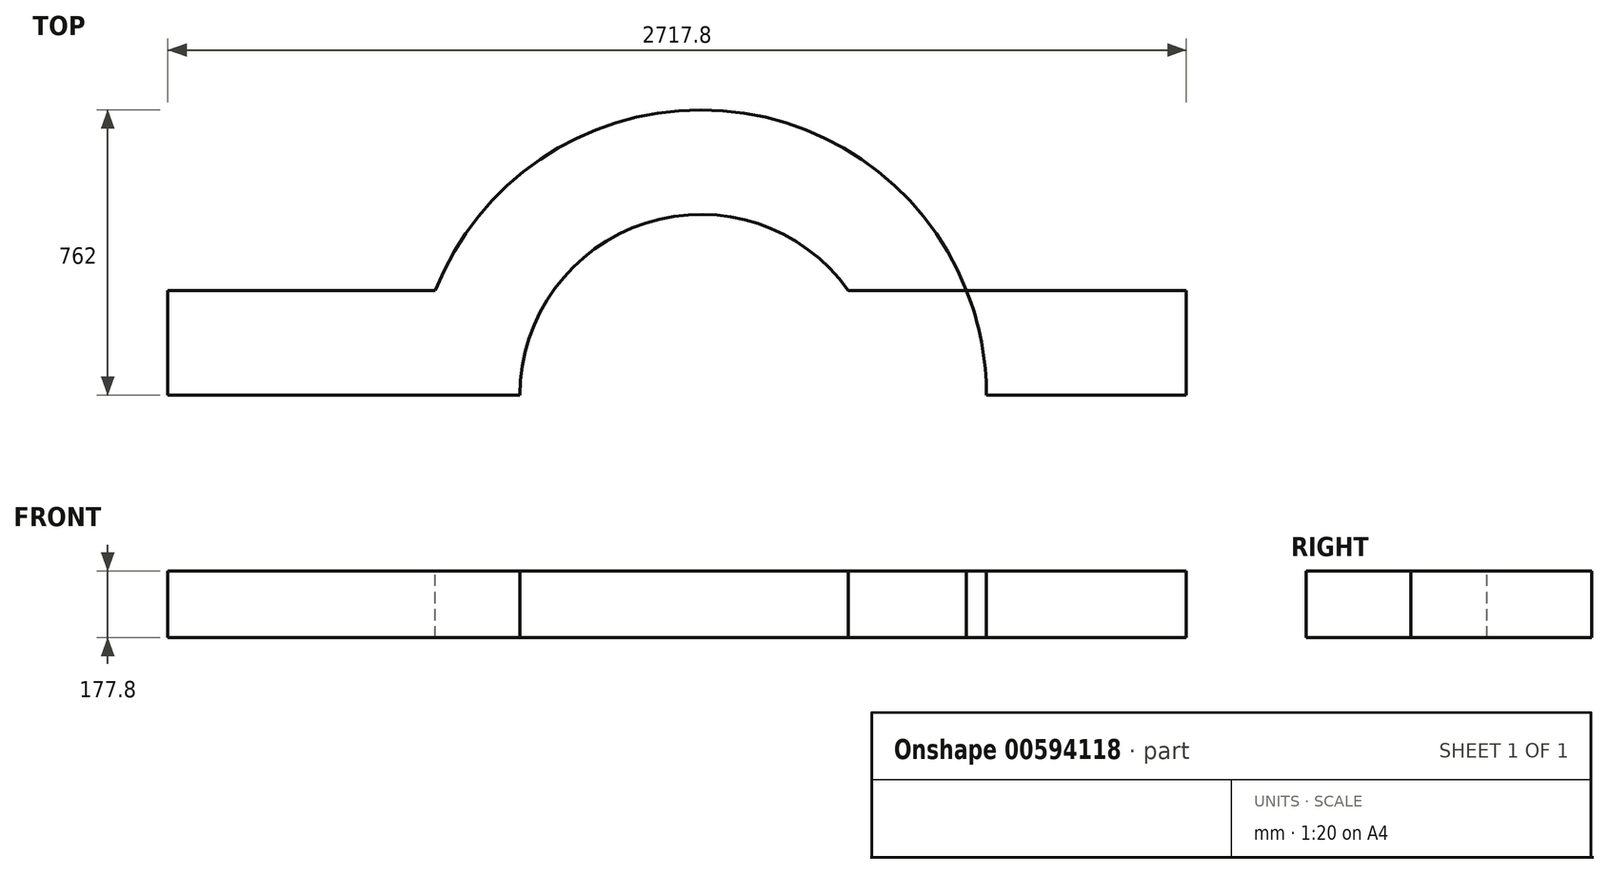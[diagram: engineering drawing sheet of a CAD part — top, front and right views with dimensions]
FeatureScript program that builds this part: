
annotation { "Feature Type Name" : "Feature", "Feature Type Description" : "" }
export const myFeature = defineFeature(function(context is Context, id is Id, definition is map)
    precondition{}
    {
        {
            var Q0;
            Q0=qCreatedBy(makeId("Top.planeOp"),FACE);
            var sketch = newSketch(context, id + "F0", { "sketchPlane" : qUnion([Q0])});
            skCircle(sketch, "E0", {"center": v(0, 0) * mm, "radius": 482.6 * mm});
            skCircle(sketch, "E1", {"center": v(0, 0) * mm, "radius": 762 * mm});
            skLineSegment(sketch, "E2.bottom", {"start": v(-1422.4, 279.4) * mm, "end": v(1295.4, 279.4) * mm});
            skLineSegment(sketch, "E2.top", {"start": v(-1422.4, 0) * mm, "end": v(1295.4, 0) * mm});
            skLineSegment(sketch, "E2.left", {"start": v(-1422.4, 279.4) * mm, "end": v(-1422.4, 0) * mm});
            skLineSegment(sketch, "E2.right", {"start": v(1295.4, 279.4) * mm, "end": v(1295.4, 0) * mm});
            skLineSegment(sketch, "E3.bottom", {"start": v(1295.4, 279.4) * mm, "end": v(1016, 279.4) * mm});
            skLineSegment(sketch, "E3.top", {"start": v(1295.4, 1320.8) * mm, "end": v(1016, 1320.8) * mm});
            skLineSegment(sketch, "E3.left", {"start": v(1295.4, 279.4) * mm, "end": v(1295.4, 1320.8) * mm});
            skLineSegment(sketch, "E3.right", {"start": v(1016, 279.4) * mm, "end": v(1016, 1320.8) * mm});
            skSolve(sketch);
        }
        {
            var Q0;
            {var subQ5=sQuery(id+"F0.wireOp",EDGE,"E2.left");Q0=makeQuery(id+"F0.imprint","IMPRINT",FACE,{"disambiguationData":[TD([[makeQuery(id+"F0.imprint","IMPRINT",EDGE,{"derivedFrom":subQ5}),1.0]])]});}
            var Q1;
            {var subQ0=sQuery(id+"F0.wireOp",EDGE,"E2.bottom");var subQ1=sQuery(id+"F0.wireOp",EDGE,"E0");var subQ2=makeQuery(id+"F0.imprint","INTERSECT",VERTEX,{"disambiguationData":[OD(1.0)],"derivedFrom":[subQ1,subQ0]});Q1=makeQuery(id+"F0.imprint","IMPRINT",FACE,{"disambiguationData":[TD([[makeQuery(id+"F0.imprint","IMPRINT",EDGE,{"disambiguationData":[TD([[subQ2,-1.0]])],"derivedFrom":subQ1}),-1.0]])]});}
            var Q2;
            {var subQ0=sQuery(id+"F0.wireOp",EDGE,"E2.bottom");var subQ1=sQuery(id+"F0.wireOp",EDGE,"E0");var subQ2=makeQuery(id+"F0.imprint","INTERSECT",VERTEX,{"disambiguationData":[OD(0.0)],"derivedFrom":[subQ1,subQ0]});Q2=makeQuery(id+"F0.imprint","IMPRINT",FACE,{"disambiguationData":[TD([[makeQuery(id+"F0.imprint","IMPRINT",EDGE,{"disambiguationData":[TD([[subQ2,1.0]])],"derivedFrom":subQ1}),-1.0]])]});}
            var Q3;
            {var subQ0=sQuery(id+"F0.wireOp",EDGE,"E2.right");Q3=makeQuery(id+"F0.imprint","IMPRINT",FACE,{"disambiguationData":[TD([[makeQuery(id+"F0.imprint","IMPRINT",EDGE,{"derivedFrom":subQ0}),-1.0]])]});}
            var Q4;
            Q4=makeQuery(id+"F0.imprint","IMPRINT",FACE,{"disambiguationData":[TD([[makeQuery(id+"F0.imprint","IMPRINT",EDGE,{"derivedFrom":sQuery(id+"F0.wireOp",EDGE,"E3.bottom")}),-1.0]])]});
            var Q5;
            {var subQ0=sQuery(id+"F0.wireOp",EDGE,"E2.bottom");var subQ1=sQuery(id+"F0.wireOp",EDGE,"E0");var subQ2=makeQuery(id+"F0.imprint","INTERSECT",VERTEX,{"disambiguationData":[OD(0.0)],"derivedFrom":[subQ1,subQ0]});Q5=makeQuery(id+"F0.imprint","IMPRINT",FACE,{"disambiguationData":[TD([[makeQuery(id+"F0.imprint","IMPRINT",EDGE,{"disambiguationData":[TD([[subQ2,-1.0]])],"derivedFrom":subQ1}),-1.0]])]});}
            extrude(context, id + "F1", {"entities" : qUnion([Q0, Q1, Q2, Q3, Q4, Q5]), "oppositeDirection" : true, "depth" : 177.8 * mm, "offsetDistance" : 25.4 * mm});
        }
    });
